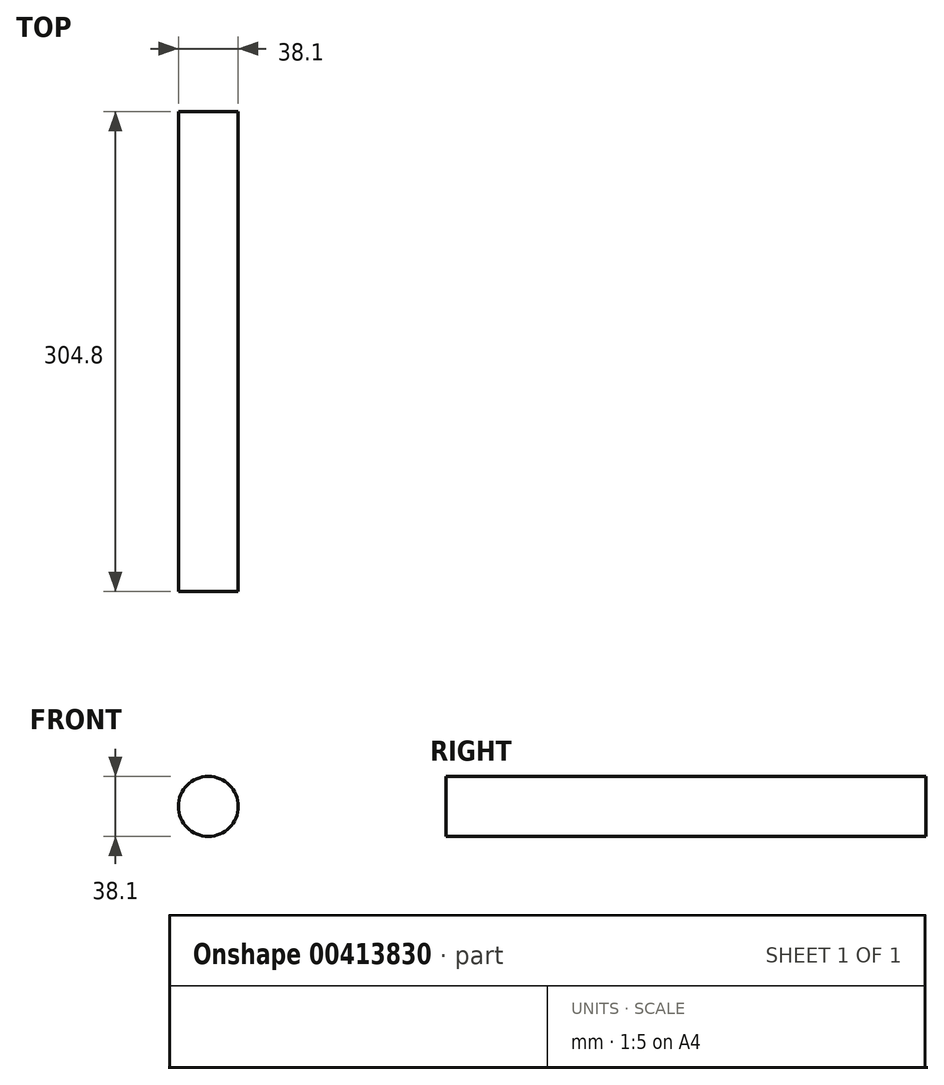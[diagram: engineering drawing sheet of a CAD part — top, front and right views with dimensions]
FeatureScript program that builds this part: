
annotation { "Feature Type Name" : "Feature", "Feature Type Description" : "" }
export const myFeature = defineFeature(function(context is Context, id is Id, definition is map)
    precondition{}
    {
        {
            var Q0;
            Q0=qCreatedBy(makeId("Front.planeOp"),FACE);
            var sketch = newSketch(context, id + "F0", { "sketchPlane" : qUnion([Q0])});
            skCircle(sketch, "E0", {"center": v(0, 0) * mm, "radius": 19.05 * mm});
            skSolve(sketch);
        }
        {
            var Q0;
            Q0=makeQuery(id+"F0.imprint","IMPRINT",FACE,{"disambiguationData":[TD([[makeQuery(id+"F0.imprint","IMPRINT",EDGE,{"derivedFrom":sQuery(id+"F0.wireOp",EDGE,"E0")}),1.0]])]});
            extrude(context, id + "F1", {"entities" : qUnion([Q0]), "depth" : 304.8 * mm});
        }
    });
